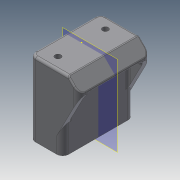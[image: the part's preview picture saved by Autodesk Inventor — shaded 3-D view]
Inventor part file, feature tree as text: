
AUTODESK INVENTOR PART (.ipt)
format: ipt  version: 2020.3 (Build 243373000, 373)  size: 268,800 bytes
history: native  units: in
note: dims shown in document units (in); Inventor stores cm internally (conversion verified against a paired STEP export)
features: fillet x8, sketch x5, extrude x3, projected_geometry x2, hole x1, mirror x1, plane x1
ambient origin geometry x8: Origin, YZ Plane, XZ Plane, XY Plane, X Axis, Y Axis, Z Axis, Center Point
bodies: Solid1 (feature_tree)
feature tree (21):
  extrude  "Extrusion1"  Depth=1.5in
  sketch  "Sketch2"  dims[d2=1.55in d3=0.0in d7=0.05in]
  extrude  "Extrusion2"  Depth=0.05in
  hole  "Hole1"  [1 undecoded]
  extrude  "Extrusion3"  Depth=0.5in
  mirror  "Mirror1"
  fillet  "Fillet4"  [1 undecoded]
  fillet  "Fillet5"  Radius=0.125in
  fillet  "Fillet6"  Radius=0.05in
  fillet  "Fillet1"  Radius=0.125in
  fillet  "Fillet2"  [1 undecoded]
  fillet  "Fillet3"  Radius=0.125in
  fillet  "Fillet7"  Radius=0.125in
  fillet  "Fillet8"  Radius=0.05in
  sketch  "Sketch1"  dims[d0=1.5in d1=0.7in]
  sketch  "Sketch3"  dims[d8=1.55in d9=1.0in d10=0.0in]
  projected_geometry  "Projected Loop1"
  sketch  "Sketch4"  dims[d11=0.5in d12=0.5in d13=0.0in]
  sketch  "Sketch5"  dims[d14=0.123in d15=0.315in d16=0.37in d17=0.25in d18=90.0deg d19=0.465in d20=0.8108in d21=0.125in d22=0.05in d23=0.125in d24=45.0deg d26=0.125in d27=0.0in d28=0.125in d29=0.05in d30=0.03in d31=0.03in d32=0.5909in d33=0.125in d34=0.7in d35=0.7in d36=1.26in]
  projected_geometry  "Projected Loop2"
  plane  "Work Plane1"
note: 3 required parameter values undecoded (feature->parameter linkage not recoverable at this tier; creation-order binding heuristic only, values carry confidence <= 0.55)
